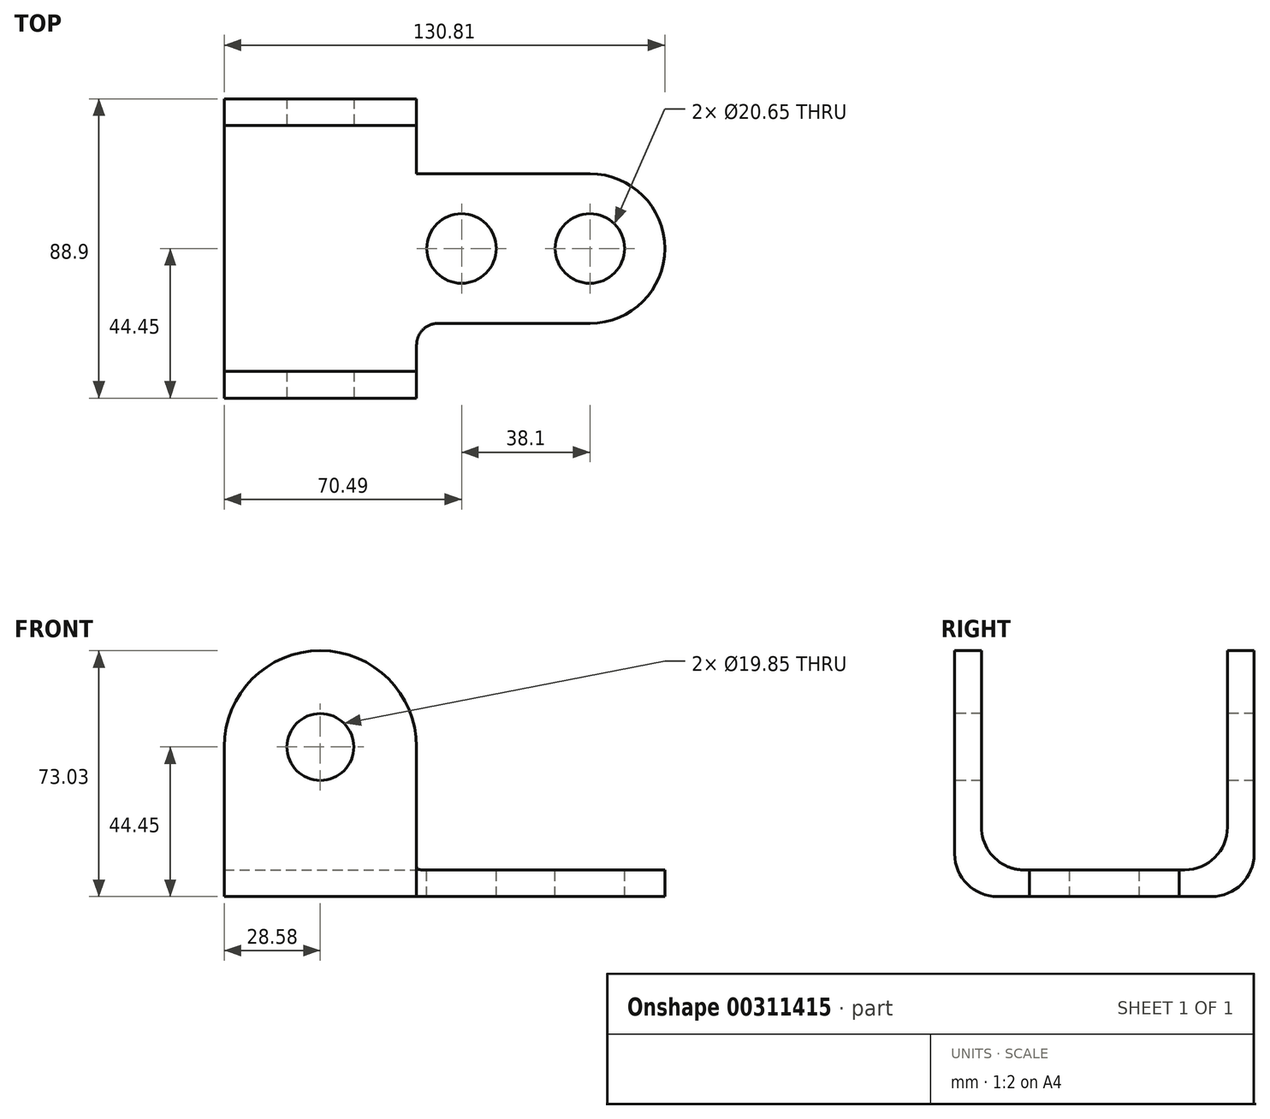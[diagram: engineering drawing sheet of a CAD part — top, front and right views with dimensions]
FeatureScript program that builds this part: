
annotation { "Feature Type Name" : "Feature", "Feature Type Description" : "" }
export const myFeature = defineFeature(function(context is Context, id is Id, definition is map)
    precondition{}
    {
        {
            var Q0;
            Q0=qCreatedBy(makeId("Front.planeOp"),FACE);
            var sketch = newSketch(context, id + "F0", { "sketchPlane" : qUnion([Q0])});
            skLineSegment(sketch, "E0", {"start": v(-28.58, 0) * mm, "end": v(28.58, 0) * mm});
            skLineSegment(sketch, "E1", {"start": v(28.58, 0) * mm, "end": v(28.58, 44.45) * mm});
            skLineSegment(sketch, "E2", {"start": v(-28.58, 0) * mm, "end": v(-28.58, 44.45) * mm});
            skArc(sketch, "E3", {"start": v(28.58, 44.45) * mm, "mid": v(0, 73.03) * mm, "end": v(-28.58, 44.45) * mm});
            skSolve(sketch);
        }
        {
            var Q0;
            Q0 = qSketchRegion(id + "F0", true);
            extrude(context, id + "F1", {"entities" : qUnion([Q0]), "endBound" : BoundingType.SYMMETRIC, "depth" : 88.9 * mm});
        }
        {
            var Q0;
            Q0=qCreatedBy(makeId("Right.planeOp"),FACE);
            var sketch = newSketch(context, id + "F2", { "sketchPlane" : qUnion([Q0])});
            skLineSegment(sketch, "E4", {"start": v(-36.51, 7.94) * mm, "end": v(36.51, 7.94) * mm});
            skLineSegment(sketch, "E5", {"start": v(36.51, 7.94) * mm, "end": v(36.51, 73.03) * mm});
            skLineSegment(sketch, "E6", {"start": v(36.51, 73.03) * mm, "end": v(-36.51, 73.03) * mm});
            skLineSegment(sketch, "E7", {"start": v(-36.51, 73.03) * mm, "end": v(-36.51, 7.94) * mm});
            skLineSegment(sketch, "E8", {"start": v(-44.45, 73.03) * mm, "end": v(44.45, 73.03) * mm});
            skSolve(sketch);
        }
        {
            var Q0;
            Q0 = qSketchRegion(id + "F2", true);
            extrude(context, id + "F3", {"entities" : qUnion([Q0]), "operationType" : NewBodyOperationType.REMOVE, "endBound" : BoundingType.THROUGH_ALL, "oppositeDirection" : true, "depth" : 25.4 * mm, "hasSecondDirection" : true, "secondDirectionBound" : SecondDirectionBoundingType.THROUGH_ALL, "secondDirectionOppositeDirection" : false, "secondDirectionDepth" : 25.4 * mm});
        }
        {
            var Q0;
            Q0=makeQuery(id+"F1.opExtrude","CAP_FACE",FACE,{"disambiguationData":[OSD([sQuery(id+"F0.wireOp",EDGE,"E0"),sQuery(id+"F0.wireOp",EDGE,"E1"),sQuery(id+"F0.wireOp",EDGE,"E2"),sQuery(id+"F0.wireOp",EDGE,"E3")])],"isStart":false});
            var sketch = newSketch(context, id + "F4", { "sketchPlane" : qUnion([Q0])});
            skCircle(sketch, "E9", {"center": v(0, 44.45) * mm, "radius": 9.92 * mm});
            skSolve(sketch);
        }
        {
            var Q0;
            Q0 = qSketchRegion(id + "F4", true);
            extrude(context, id + "F5", {"entities" : qUnion([Q0]), "operationType" : NewBodyOperationType.REMOVE, "endBound" : BoundingType.THROUGH_ALL, "oppositeDirection" : true, "depth" : 25.4 * mm});
        }
        {
            var Q0;
            Q0=qCreatedBy(makeId("Top.planeOp"),FACE);
            var sketch = newSketch(context, id + "F6", { "sketchPlane" : qUnion([Q0])});
            skLineSegment(sketch, "E10.0", {"start": v(28.58, 36.51) * mm, "end": v(28.58, -36.51) * mm});
            skLineSegment(sketch, "E11", {"start": v(28.58, 22.22) * mm, "end": v(80, 22.23) * mm});
            skLineSegment(sketch, "E12", {"start": v(28.58, -22.23) * mm, "end": v(80, -22.22) * mm});
            skArc(sketch, "E13", {"start": v(80, -22.22) * mm, "mid": v(102.23, 0) * mm, "end": v(80, 22.23) * mm});
            skLineSegment(sketch, "E14", {"start": v(80, 0) * mm, "end": v(28.58, 0) * mm, "construction": true});
            skSolve(sketch);
        }
        {
            var Q0;
            Q0 = qSketchRegion(id + "F6", true);
            extrude(context, id + "F7", {"entities" : qUnion([Q0]), "operationType" : NewBodyOperationType.ADD, "depth" : 7.94 * mm});
        }
        {
            var Q0;
            Q0=makeQuery(id+"F7.boolean.opBoolean","MERGE",FACE,{"derivedFrom":[makeQuery(id+"F3.boolean.opBoolean","COPY",FACE,{"derivedFrom":makeQuery(id+"F3.opExtrude","SWEPT_FACE",FACE,{"disambiguationData":[OSD([sQuery(id+"F2.wireOp",EDGE,"E4")])]})}),makeQuery(id+"F7.opExtrude","CAP_FACE",FACE,{"disambiguationData":[OSD([sQuery(id+"F6.wireOp",EDGE,"E10.0"),sQuery(id+"F6.wireOp",EDGE,"E11"),sQuery(id+"F6.wireOp",EDGE,"E12"),sQuery(id+"F6.wireOp",EDGE,"E13")])],"isStart":false})]});
            var sketch = newSketch(context, id + "F8", { "sketchPlane" : qUnion([Q0])});
            skCircle(sketch, "E15", {"center": v(41.9, 0) * mm, "radius": 10.33 * mm});
            skCircle(sketch, "E16", {"center": v(80, 0) * mm, "radius": 10.33 * mm});
            skSolve(sketch);
        }
        {
            var Q0;
            Q0 = qSketchRegion(id + "F8", true);
            extrude(context, id + "F9", {"entities" : qUnion([Q0]), "operationType" : NewBodyOperationType.REMOVE, "endBound" : BoundingType.THROUGH_ALL, "oppositeDirection" : true, "depth" : 25.4 * mm});
        }
        {
            var Q0;
            Q0=makeQuery(id+"F7.opExtrude","SWEPT_EDGE",EDGE,{"disambiguationData":[OSD([sQuery(id+"F6.wireOp",EDGE,"E10.0"),sQuery(id+"F6.wireOp",EDGE,"E12")])]});
            var Q1;
            Q1=makeQuery(id+"F7.opExtrude","SWEPT_EDGE",EDGE,{"disambiguationData":[OSD([sQuery(id+"F6.wireOp",EDGE,"E10.0"),sQuery(id+"F6.wireOp",EDGE,"E11")])]});
            fillet(context, id + "F10", {"entities" : qUnion([Q0, Q1]), "radius" : 6.35 * mm, "tangentPropagation" : true, "allowEdgeOverflow" : false});
        }
        {
            var Q0;
            Q0=makeQuery(id+"F3.boolean.opBoolean","COPY",EDGE,{"derivedFrom":makeQuery(id+"F3.opExtrude","SWEPT_EDGE",EDGE,{"disambiguationData":[OSD([sQuery(id+"F2.wireOp",EDGE,"E4"),sQuery(id+"F2.wireOp",EDGE,"E7")])]})});
            var Q1;
            Q1=makeQuery(id+"F3.boolean.opBoolean","COPY",EDGE,{"derivedFrom":makeQuery(id+"F3.opExtrude","SWEPT_EDGE",EDGE,{"disambiguationData":[OSD([sQuery(id+"F2.wireOp",EDGE,"E4"),sQuery(id+"F2.wireOp",EDGE,"E5")])]})});
            var Q2;
            Q2=makeQuery(id+"F1.opExtrude","CAP_EDGE",EDGE,{"disambiguationData":[OSD([sQuery(id+"F0.wireOp",EDGE,"E0")])],"isStart":false});
            var Q3;
            Q3=makeQuery(id+"F1.opExtrude","CAP_EDGE",EDGE,{"disambiguationData":[OSD([sQuery(id+"F0.wireOp",EDGE,"E0")])],"isStart":true});
            fillet(context, id + "F11", {"entities" : qUnion([Q0, Q1, Q2, Q3]), "radius" : 12.7 * mm, "tangentPropagation" : true, "allowEdgeOverflow" : false});
        }
    });
